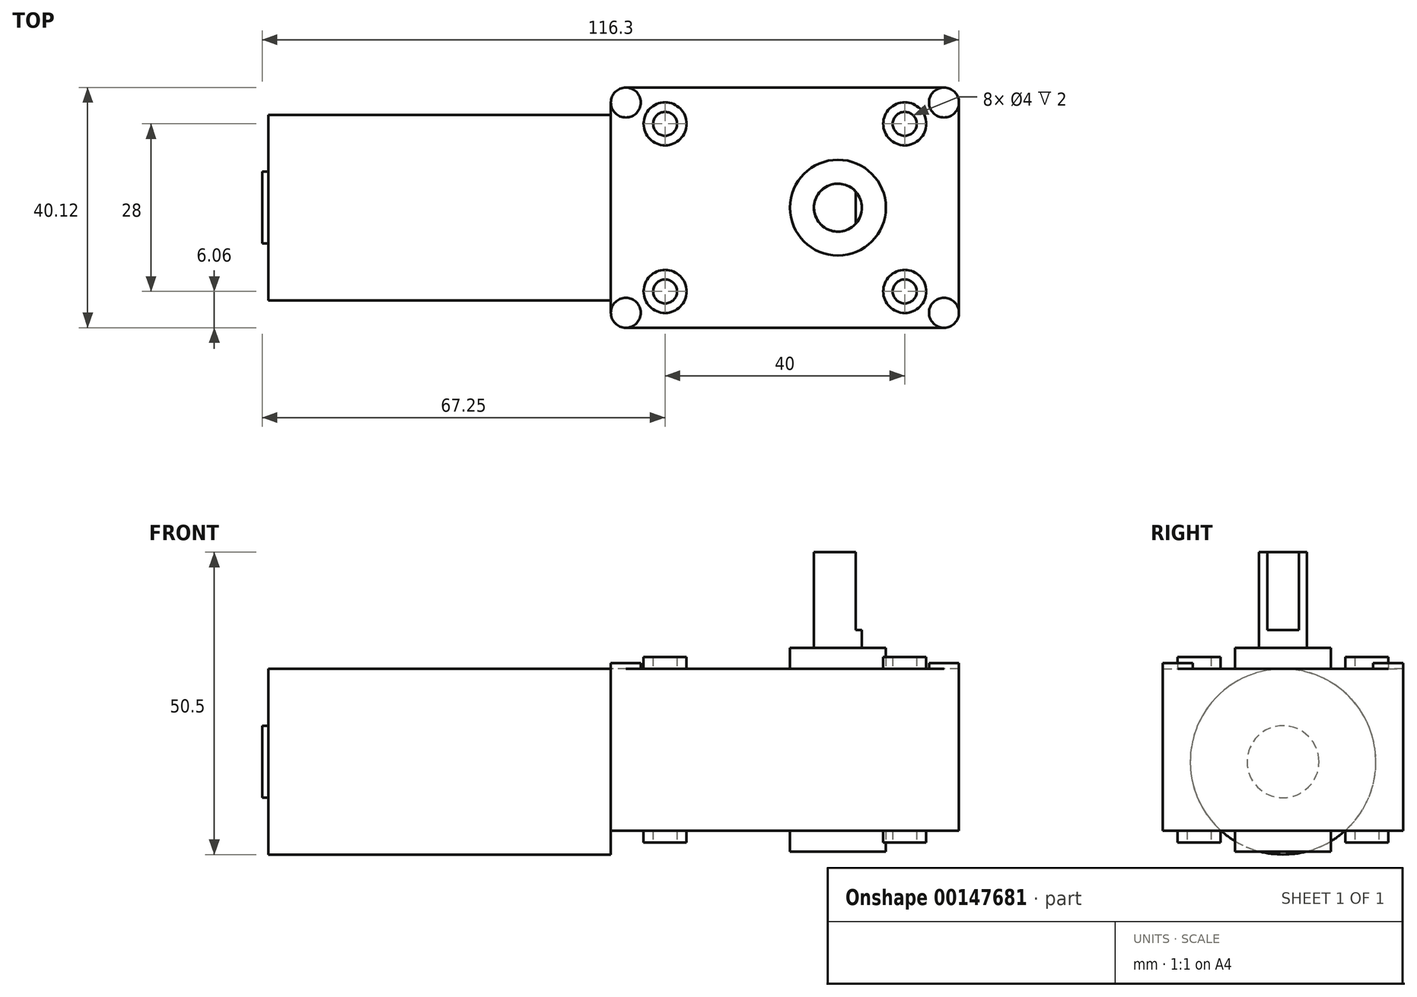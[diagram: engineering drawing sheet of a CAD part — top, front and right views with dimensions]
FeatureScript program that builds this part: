
annotation { "Feature Type Name" : "Feature", "Feature Type Description" : "" }
export const myFeature = defineFeature(function(context is Context, id is Id, definition is map)
    precondition{}
    {
        {
            var Q0;
            Q0=qCreatedBy(makeId("Top.planeOp"),FACE);
            var sketch = newSketch(context, id + "F0", { "sketchPlane" : qUnion([Q0])});
            skLineSegment(sketch, "E0.bottom", {"start": v(0, 0) * mm, "end": v(58.1, 0) * mm});
            skLineSegment(sketch, "E0.top", {"start": v(0, -40.12) * mm, "end": v(58.1, -40.12) * mm});
            skLineSegment(sketch, "E0.left", {"start": v(0, 0) * mm, "end": v(0, -40.12) * mm});
            skLineSegment(sketch, "E0.right", {"start": v(58.1, 0) * mm, "end": v(58.1, -40.12) * mm});
            skSolve(sketch);
        }
        {
            var Q0;
            Q0=qSketchRegion(id+"F0",true);
            extrude(context, id + "F1", {"entities" : qUnion([Q0]), "endBound" : BoundingType.SYMMETRIC, "depth" : 27 * mm});
        }
        {
            var Q0;
            Q0=makeQuery(id+"F1.opExtrude","SWEPT_EDGE",EDGE,{"disambiguationData":[OSD([sQuery(id+"F0.wireOp",EDGE,"E0.top"),sQuery(id+"F0.wireOp",EDGE,"E0.left")])]});
            var Q1;
            Q1=makeQuery(id+"F1.opExtrude","SWEPT_EDGE",EDGE,{"disambiguationData":[OSD([sQuery(id+"F0.wireOp",EDGE,"E0.top"),sQuery(id+"F0.wireOp",EDGE,"E0.right")])]});
            var Q2;
            Q2=makeQuery(id+"F1.opExtrude","SWEPT_EDGE",EDGE,{"disambiguationData":[OSD([sQuery(id+"F0.wireOp",EDGE,"E0.bottom"),sQuery(id+"F0.wireOp",EDGE,"E0.right")])]});
            var Q3;
            Q3=makeQuery(id+"F1.opExtrude","SWEPT_EDGE",EDGE,{"disambiguationData":[OSD([sQuery(id+"F0.wireOp",EDGE,"E0.bottom"),sQuery(id+"F0.wireOp",EDGE,"E0.left")])]});
            fillet(context, id + "F2", {"entities" : qUnion([Q0, Q1, Q2, Q3]), "radius" : 2.5 * mm, "tangentPropagation" : true, "allowEdgeOverflow" : false});
        }
        {
            var Q0;
            Q0=makeQuery(id+"F1.opExtrude","CAP_FACE",FACE,{"disambiguationData":[OSD([sQuery(id+"F0.wireOp",EDGE,"E0.bottom"),sQuery(id+"F0.wireOp",EDGE,"E0.top"),sQuery(id+"F0.wireOp",EDGE,"E0.left"),sQuery(id+"F0.wireOp",EDGE,"E0.right")])],"isStart":false});
            var sketch = newSketch(context, id + "F3", { "sketchPlane" : qUnion([Q0])});
            skCircle(sketch, "E1", {"center": v(55.6, -2.5) * mm, "radius": 2.5 * mm});
            skCircle(sketch, "E2", {"center": v(55.6, -37.62) * mm, "radius": 2.5 * mm});
            skCircle(sketch, "E3", {"center": v(2.5, -2.5) * mm, "radius": 2.5 * mm});
            skCircle(sketch, "E4", {"center": v(2.5, -37.62) * mm, "radius": 2.5 * mm});
            skSolve(sketch);
        }
        {
            var Q0;
            Q0=qSketchRegion(id+"F3",true);
            extrude(context, id + "F4", {"entities" : qUnion([Q0]), "operationType" : NewBodyOperationType.ADD, "depth" : 1 * mm});
        }
        {
            var Q0;
            Q0=qCreatedBy(makeId("Top.planeOp"),FACE);
            var sketch = newSketch(context, id + "F5", { "sketchPlane" : qUnion([Q0])});
            skLineSegment(sketch, "E5", {"start": v(0, -20.06) * mm, "end": v(37.9, -20.06) * mm, "construction": true});
            skCircle(sketch, "E6", {"center": v(37.9, -20.06) * mm, "radius": 8 * mm});
            skSolve(sketch);
        }
        {
            var Q0;
            Q0=qSketchRegion(id+"F5",true);
            extrude(context, id + "F6", {"entities" : qUnion([Q0]), "operationType" : NewBodyOperationType.ADD, "endBound" : BoundingType.SYMMETRIC, "depth" : 34 * mm});
        }
        {
            var Q0;
            Q0=makeQuery(id+"F6.opExtrude","CAP_FACE",FACE,{"disambiguationData":[OSD([sQuery(id+"F5.wireOp",EDGE,"E6")])],"isStart":false});
            var sketch = newSketch(context, id + "F7", { "sketchPlane" : qUnion([Q0])});
            skCircle(sketch, "E7", {"center": v(37.9, -20.06) * mm, "radius": 4 * mm});
            skSolve(sketch);
        }
        {
            var Q0;
            Q0=qSketchRegion(id+"F7",true);
            extrude(context, id + "F8", {"entities" : qUnion([Q0]), "operationType" : NewBodyOperationType.ADD, "depth" : 16 * mm});
        }
        {
            var Q0;
            Q0=makeQuery(id+"F8.opExtrude","CAP_FACE",FACE,{"disambiguationData":[OSD([sQuery(id+"F7.wireOp",EDGE,"E7")])],"isStart":false});
            var sketch = newSketch(context, id + "F9", { "sketchPlane" : qUnion([Q0])});
            skLineSegment(sketch, "E8.bottom", {"start": v(40.9, -17.41) * mm, "end": v(41.9, -17.41) * mm});
            skLineSegment(sketch, "E8.top", {"start": v(40.9, -22.7) * mm, "end": v(41.9, -22.7) * mm});
            skLineSegment(sketch, "E8.left", {"start": v(40.9, -17.41) * mm, "end": v(40.9, -22.7) * mm});
            skLineSegment(sketch, "E8.right", {"start": v(41.9, -17.41) * mm, "end": v(41.9, -22.7) * mm});
            skSolve(sketch);
        }
        {
            var Q0;
            Q0=qSketchRegion(id+"F9",true);
            extrude(context, id + "F10", {"entities" : qUnion([Q0]), "operationType" : NewBodyOperationType.REMOVE, "oppositeDirection" : true, "depth" : 13 * mm});
        }
        {
            var Q0;
            Q0=qCreatedBy(makeId("Top.planeOp"),FACE);
            var sketch = newSketch(context, id + "F11", { "sketchPlane" : qUnion([Q0])});
            skLineSegment(sketch, "E9.bottom", {"start": v(9.05, -6.06) * mm, "end": v(49.05, -6.06) * mm, "construction": true});
            skLineSegment(sketch, "E9.top", {"start": v(9.05, -34.06) * mm, "end": v(49.05, -34.06) * mm, "construction": true});
            skLineSegment(sketch, "E9.left", {"start": v(9.05, -6.06) * mm, "end": v(9.05, -34.06) * mm, "construction": true});
            skLineSegment(sketch, "E9.right", {"start": v(49.05, -6.06) * mm, "end": v(49.05, -34.06) * mm, "construction": true});
            skCircle(sketch, "E10", {"center": v(49.05, -6.06) * mm, "radius": 2 * mm});
            skCircle(sketch, "E11", {"center": v(49.05, -6.06) * mm, "radius": 3.59 * mm});
            skLineSegment(sketch, "E12", {"start": v(49.05, -20.06) * mm, "end": v(58.1, -20.06) * mm, "construction": true});
            skLineSegment(sketch, "E13", {"start": v(0, -20.06) * mm, "end": v(9.05, -20.06) * mm, "construction": true});
            skCircle(sketch, "E14", {"center": v(49.05, -34.06) * mm, "radius": 2 * mm});
            skCircle(sketch, "E15", {"center": v(49.05, -34.06) * mm, "radius": 3.59 * mm});
            skCircle(sketch, "E16", {"center": v(9.05, -34.06) * mm, "radius": 2 * mm});
            skCircle(sketch, "E17", {"center": v(9.05, -34.06) * mm, "radius": 3.59 * mm});
            skCircle(sketch, "E18", {"center": v(9.05, -6.06) * mm, "radius": 2 * mm});
            skCircle(sketch, "E19", {"center": v(9.05, -6.06) * mm, "radius": 3.59 * mm});
            skSolve(sketch);
        }
        {
            var Q0;
            Q0=qSketchRegion(id+"F11",true);
            extrude(context, id + "F12", {"entities" : qUnion([Q0]), "operationType" : NewBodyOperationType.ADD, "endBound" : BoundingType.SYMMETRIC, "depth" : 31 * mm});
        }
        {
            var Q0;
            Q0=makeQuery(id+"F1.opExtrude","SWEPT_FACE",FACE,{"disambiguationData":[OSD([sQuery(id+"F0.wireOp",EDGE,"E0.left")])]});
            var sketch = newSketch(context, id + "F13", { "sketchPlane" : qUnion([Q0])});
            skLineSegment(sketch, "E20", {"start": v(20.06, 13.5) * mm, "end": v(20.06, -2) * mm, "construction": true});
            skCircle(sketch, "E21", {"center": v(20.06, -2) * mm, "radius": 15.5 * mm});
            skSolve(sketch);
        }
        {
            var Q0;
            Q0=qSketchRegion(id+"F13",true);
            extrude(context, id + "F14", {"entities" : qUnion([Q0]), "operationType" : NewBodyOperationType.ADD, "depth" : 57.2 * mm});
        }
        {
            var Q0;
            Q0=makeQuery(id+"F14.opExtrude","CAP_FACE",FACE,{"disambiguationData":[OSD([sQuery(id+"F13.wireOp",EDGE,"E21")])],"isStart":false});
            var sketch = newSketch(context, id + "F15", { "sketchPlane" : qUnion([Q0])});
            skCircle(sketch, "E22", {"center": v(20.06, -2) * mm, "radius": 6 * mm});
            skSolve(sketch);
        }
        {
            var Q0;
            Q0=qSketchRegion(id+"F15",true);
            extrude(context, id + "F16", {"entities" : qUnion([Q0]), "operationType" : NewBodyOperationType.ADD, "depth" : 1 * mm});
        }
    });
